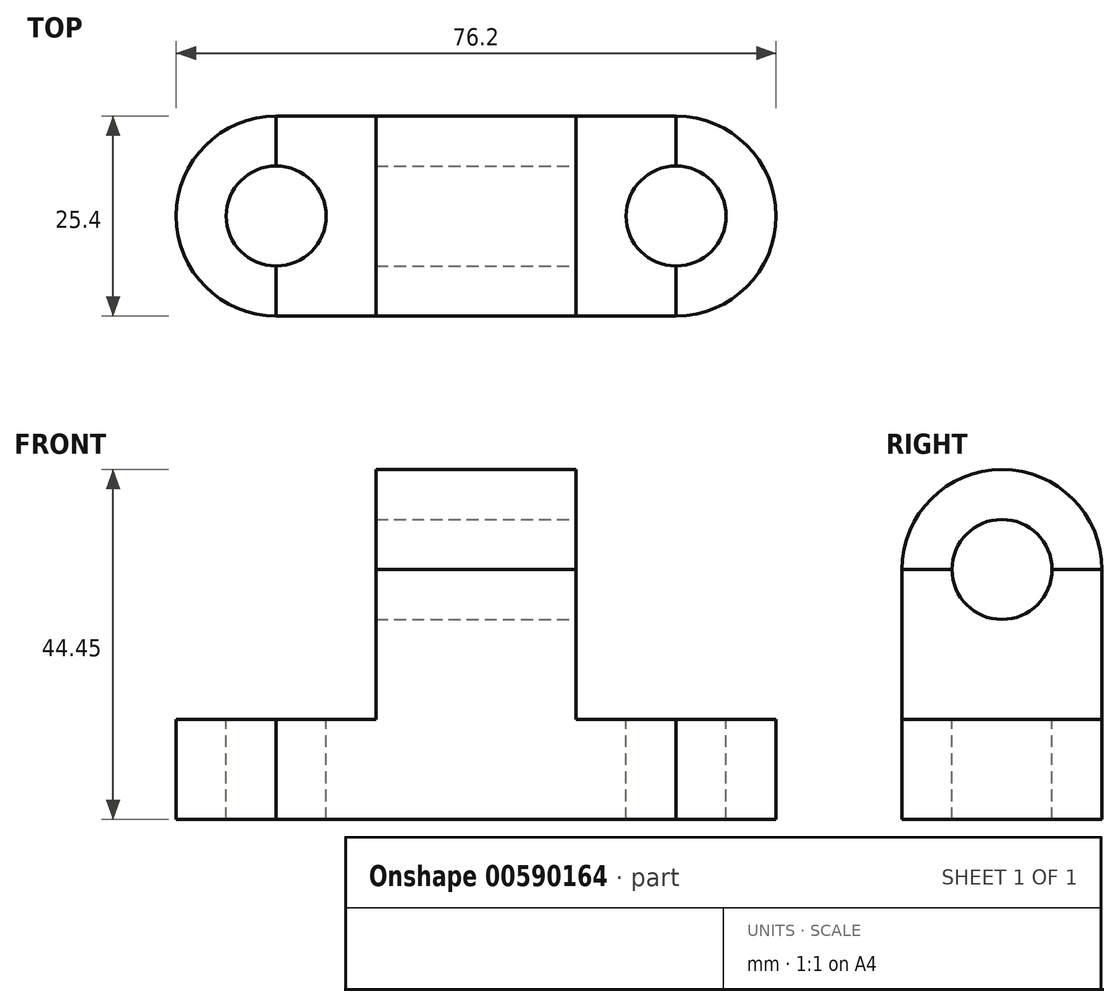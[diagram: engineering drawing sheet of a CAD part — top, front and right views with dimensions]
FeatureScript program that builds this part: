
annotation { "Feature Type Name" : "Feature", "Feature Type Description" : "" }
export const myFeature = defineFeature(function(context is Context, id is Id, definition is map)
    precondition{}
    {
        {
            var Q0;
            Q0=qCreatedBy(makeId("Front.planeOp"),FACE);
            var sketch = newSketch(context, id + "F0", { "sketchPlane" : qUnion([Q0])});
            skLineSegment(sketch, "E0", {"start": v(-76.52, 30.01) * mm, "end": v(-76.52, 17.31) * mm});
            skLineSegment(sketch, "E1", {"start": v(-76.52, 17.31) * mm, "end": v(-25.72, 17.31) * mm});
            skLineSegment(sketch, "E2", {"start": v(-25.72, 17.31) * mm, "end": v(-25.72, 30.01) * mm});
            skLineSegment(sketch, "E3", {"start": v(-25.72, 30.01) * mm, "end": v(-38.42, 30.01) * mm});
            skLineSegment(sketch, "E4", {"start": v(-38.42, 30.01) * mm, "end": v(-38.42, 49.06) * mm});
            skLineSegment(sketch, "E5", {"start": v(-38.42, 49.06) * mm, "end": v(-63.82, 49.06) * mm});
            skLineSegment(sketch, "E6", {"start": v(-63.82, 49.06) * mm, "end": v(-63.82, 30.01) * mm});
            skLineSegment(sketch, "E7", {"start": v(-63.82, 30.01) * mm, "end": v(-76.52, 30.01) * mm});
            skSolve(sketch);
        }
        {
            var Q0;
            Q0 = qSketchRegion(id + "F0", true);
            extrude(context, id + "F1", {"entities" : qUnion([Q0]), "depth" : 25.4 * mm, "offsetDistance" : 25.4 * mm});
        }
        {
            var Q0;
            Q0=makeQuery(id+"F1.opExtrude","SWEPT_FACE",FACE,{"disambiguationData":[OSD([sQuery(id+"F0.wireOp",EDGE,"E6")])]});
            var sketch = newSketch(context, id + "F2", { "sketchPlane" : qUnion([Q0])});
            skArc(sketch, "E8", {"start": v(25.4, 49.06) * mm, "mid": v(12.7, 61.76) * mm, "end": v(0, 49.06) * mm});
            skLineSegment(sketch, "E9", {"start": v(0, 49.06) * mm, "end": v(25.4, 49.06) * mm});
            skSolve(sketch);
        }
        {
            var Q0;
            Q0 = qSketchRegion(id + "F2", true);
            extrude(context, id + "F3", {"entities" : qUnion([Q0]), "oppositeDirection" : true, "depth" : 25.4 * mm, "offsetDistance" : 25.4 * mm});
        }
        {
            var Q0;
            Q0=makeQuery(id+"F3.opExtrude","CAP_FACE",FACE,{"disambiguationData":[OSD([sQuery(id+"F2.wireOp",EDGE,"E8"),sQuery(id+"F2.wireOp",EDGE,"E9")])],"isStart":false});
            var sketch = newSketch(context, id + "F4", { "sketchPlane" : qUnion([Q0])});
            skCircle(sketch, "E10", {"center": v(-12.7, 49.06) * mm, "radius": 6.35 * mm});
            skSolve(sketch);
        }
        {
            var Q0;
            {var subQ0=sQuery(id+"F4.wireOp",EDGE,"E10");var subQ1=makeQuery(id+"F3.opExtrude","CAP_EDGE",EDGE,{"disambiguationData":[OSD([sQuery(id+"F2.wireOp",EDGE,"E9")])],"isStart":false});var subQ2=makeQuery(id+"F4.imprint","INTERSECT",VERTEX,{"disambiguationData":[OD(0.0)],"derivedFrom":[subQ1,subQ0]});Q0=makeQuery(id+"F4.imprint","IMPRINT",FACE,{"disambiguationData":[TD([[makeQuery(id+"F4.imprint","IMPRINT",EDGE,{"disambiguationData":[TD([[subQ2,-1.0]])],"derivedFrom":subQ0}),1.0]])]});}
            extrude(context, id + "F5", {"entities" : qUnion([Q0]), "operationType" : NewBodyOperationType.REMOVE, "oppositeDirection" : true, "depth" : 25.4 * mm, "offsetDistance" : 25.4 * mm});
        }
        {
            var Q0;
            Q0=makeQuery(id+"F1.opExtrude","SWEPT_FACE",FACE,{"disambiguationData":[OSD([sQuery(id+"F0.wireOp",EDGE,"E4")])]});
            var sketch = newSketch(context, id + "F6", { "sketchPlane" : qUnion([Q0])});
            skCircle(sketch, "E11", {"center": v(-12.7, 49.06) * mm, "radius": 6.35 * mm});
            skSolve(sketch);
        }
        {
            var Q0;
            {var subQ0=sQuery(id+"F6.wireOp",EDGE,"E11");var subQ1=makeQuery(id+"F1.opExtrude","SWEPT_EDGE",EDGE,{"disambiguationData":[OSD([sQuery(id+"F0.wireOp",EDGE,"E4"),sQuery(id+"F0.wireOp",EDGE,"E5")])]});var subQ2=makeQuery(id+"F6.imprint","INTERSECT",VERTEX,{"disambiguationData":[OD(0.0)],"derivedFrom":[subQ1,subQ0]});Q0=makeQuery(id+"F6.imprint","IMPRINT",FACE,{"disambiguationData":[TD([[makeQuery(id+"F6.imprint","IMPRINT",EDGE,{"disambiguationData":[TD([[subQ2,1.0]])],"derivedFrom":subQ0}),1.0]])]});}
            extrude(context, id + "F7", {"entities" : qUnion([Q0]), "operationType" : NewBodyOperationType.REMOVE, "oppositeDirection" : true, "depth" : 25.4 * mm, "offsetDistance" : 25.4 * mm});
        }
        {
            var Q0;
            Q0=makeQuery(id+"F1.opExtrude","SWEPT_FACE",FACE,{"disambiguationData":[OSD([sQuery(id+"F0.wireOp",EDGE,"E3")])]});
            var sketch = newSketch(context, id + "F8", { "sketchPlane" : qUnion([Q0])});
            skArc(sketch, "E12", {"start": v(-25.72, -25.4) * mm, "mid": v(-13.02, -12.7) * mm, "end": v(-25.72, 0) * mm});
            skLineSegment(sketch, "E13", {"start": v(-25.72, 0) * mm, "end": v(-25.72, -25.4) * mm});
            skSolve(sketch);
        }
        {
            var Q0;
            Q0 = qSketchRegion(id + "F8", true);
            extrude(context, id + "F9", {"entities" : qUnion([Q0]), "oppositeDirection" : true, "depth" : 12.7 * mm, "offsetDistance" : 25.4 * mm});
        }
        {
            var Q0;
            Q0=makeQuery(id+"F1.opExtrude","SWEPT_FACE",FACE,{"disambiguationData":[OSD([sQuery(id+"F0.wireOp",EDGE,"E7")])]});
            var sketch = newSketch(context, id + "F10", { "sketchPlane" : qUnion([Q0])});
            skArc(sketch, "E14", {"start": v(-76.52, 0) * mm, "mid": v(-89.22, -12.7) * mm, "end": v(-76.52, -25.4) * mm});
            skLineSegment(sketch, "E15", {"start": v(-76.52, 0) * mm, "end": v(-76.52, -25.4) * mm});
            skSolve(sketch);
        }
        {
            var Q0;
            Q0 = qSketchRegion(id + "F10", true);
            extrude(context, id + "F11", {"entities" : qUnion([Q0]), "oppositeDirection" : true, "depth" : 12.7 * mm, "offsetDistance" : 25.4 * mm});
        }
        {
            var Q0;
            Q0=makeQuery(id+"F9.opExtrude","CAP_FACE",FACE,{"disambiguationData":[OSD([sQuery(id+"F8.wireOp",EDGE,"E12"),sQuery(id+"F8.wireOp",EDGE,"E13")])],"isStart":true});
            var sketch = newSketch(context, id + "F12", { "sketchPlane" : qUnion([Q0])});
            skCircle(sketch, "E16", {"center": v(-25.72, -12.7) * mm, "radius": 6.35 * mm});
            skSolve(sketch);
        }
        {
            var Q0;
            {var subQ0=sQuery(id+"F12.wireOp",EDGE,"E16");var subQ1=makeQuery(id+"F9.opExtrude","CAP_EDGE",EDGE,{"disambiguationData":[OSD([sQuery(id+"F8.wireOp",EDGE,"E13")])],"isStart":true});var subQ2=makeQuery(id+"F12.imprint","INTERSECT",VERTEX,{"disambiguationData":[OD(0.0)],"derivedFrom":[subQ1,subQ0]});Q0=makeQuery(id+"F12.imprint","IMPRINT",FACE,{"disambiguationData":[TD([[makeQuery(id+"F12.imprint","IMPRINT",EDGE,{"disambiguationData":[TD([[subQ2,1.0]])],"derivedFrom":subQ0}),1.0]])]});}
            extrude(context, id + "F13", {"entities" : qUnion([Q0]), "operationType" : NewBodyOperationType.REMOVE, "oppositeDirection" : true, "depth" : 12.7 * mm, "offsetDistance" : 25.4 * mm});
        }
        {
            var Q0;
            Q0=makeQuery(id+"F1.opExtrude","SWEPT_FACE",FACE,{"disambiguationData":[OSD([sQuery(id+"F0.wireOp",EDGE,"E3")])]});
            var sketch = newSketch(context, id + "F14", { "sketchPlane" : qUnion([Q0])});
            skCircle(sketch, "E17", {"center": v(-25.72, -12.7) * mm, "radius": 6.35 * mm});
            skSolve(sketch);
        }
        {
            var Q0;
            {var subQ0=sQuery(id+"F14.wireOp",EDGE,"E17");var subQ1=makeQuery(id+"F1.opExtrude","SWEPT_EDGE",EDGE,{"disambiguationData":[OSD([sQuery(id+"F0.wireOp",EDGE,"E2"),sQuery(id+"F0.wireOp",EDGE,"E3")])]});var subQ2=makeQuery(id+"F14.imprint","INTERSECT",VERTEX,{"disambiguationData":[OD(0.0)],"derivedFrom":[subQ1,subQ0]});Q0=makeQuery(id+"F14.imprint","IMPRINT",FACE,{"disambiguationData":[TD([[makeQuery(id+"F14.imprint","IMPRINT",EDGE,{"disambiguationData":[TD([[subQ2,-1.0]])],"derivedFrom":subQ0}),1.0]])]});}
            extrude(context, id + "F15", {"entities" : qUnion([Q0]), "operationType" : NewBodyOperationType.REMOVE, "oppositeDirection" : true, "depth" : 12.7 * mm, "offsetDistance" : 25.4 * mm});
        }
        {
            var Q0;
            Q0=makeQuery(id+"F11.opExtrude","CAP_FACE",FACE,{"disambiguationData":[OSD([sQuery(id+"F10.wireOp",EDGE,"E14"),sQuery(id+"F10.wireOp",EDGE,"E15")])],"isStart":true});
            var sketch = newSketch(context, id + "F16", { "sketchPlane" : qUnion([Q0])});
            skCircle(sketch, "E18", {"center": v(-76.52, -12.7) * mm, "radius": 6.35 * mm});
            skSolve(sketch);
        }
        {
            var Q0;
            {var subQ0=sQuery(id+"F16.wireOp",EDGE,"E18");var subQ1=makeQuery(id+"F11.opExtrude","CAP_EDGE",EDGE,{"disambiguationData":[OSD([sQuery(id+"F10.wireOp",EDGE,"E15")])],"isStart":true});var subQ2=makeQuery(id+"F16.imprint","INTERSECT",VERTEX,{"disambiguationData":[OD(0.0)],"derivedFrom":[subQ1,subQ0]});Q0=makeQuery(id+"F16.imprint","IMPRINT",FACE,{"disambiguationData":[TD([[makeQuery(id+"F16.imprint","IMPRINT",EDGE,{"disambiguationData":[TD([[subQ2,-1.0]])],"derivedFrom":subQ0}),1.0]])]});}
            extrude(context, id + "F17", {"entities" : qUnion([Q0]), "operationType" : NewBodyOperationType.REMOVE, "oppositeDirection" : true, "depth" : 12.7 * mm, "offsetDistance" : 25.4 * mm});
        }
        {
            var Q0;
            Q0=makeQuery(id+"F1.opExtrude","SWEPT_FACE",FACE,{"disambiguationData":[OSD([sQuery(id+"F0.wireOp",EDGE,"E7")])]});
            var sketch = newSketch(context, id + "F18", { "sketchPlane" : qUnion([Q0])});
            skCircle(sketch, "E19", {"center": v(-76.52, -12.7) * mm, "radius": 6.35 * mm});
            skSolve(sketch);
        }
        {
            var Q0;
            {var subQ0=sQuery(id+"F18.wireOp",EDGE,"E19");var subQ1=makeQuery(id+"F1.opExtrude","SWEPT_EDGE",EDGE,{"disambiguationData":[OSD([sQuery(id+"F0.wireOp",EDGE,"E0"),sQuery(id+"F0.wireOp",EDGE,"E7")])]});var subQ2=makeQuery(id+"F18.imprint","INTERSECT",VERTEX,{"disambiguationData":[OD(0.0)],"derivedFrom":[subQ1,subQ0]});Q0=makeQuery(id+"F18.imprint","IMPRINT",FACE,{"disambiguationData":[TD([[makeQuery(id+"F18.imprint","IMPRINT",EDGE,{"disambiguationData":[TD([[subQ2,1.0]])],"derivedFrom":subQ0}),1.0]])]});}
            extrude(context, id + "F19", {"entities" : qUnion([Q0]), "operationType" : NewBodyOperationType.REMOVE, "oppositeDirection" : true, "depth" : 12.7 * mm, "offsetDistance" : 25.4 * mm});
        }
    });
